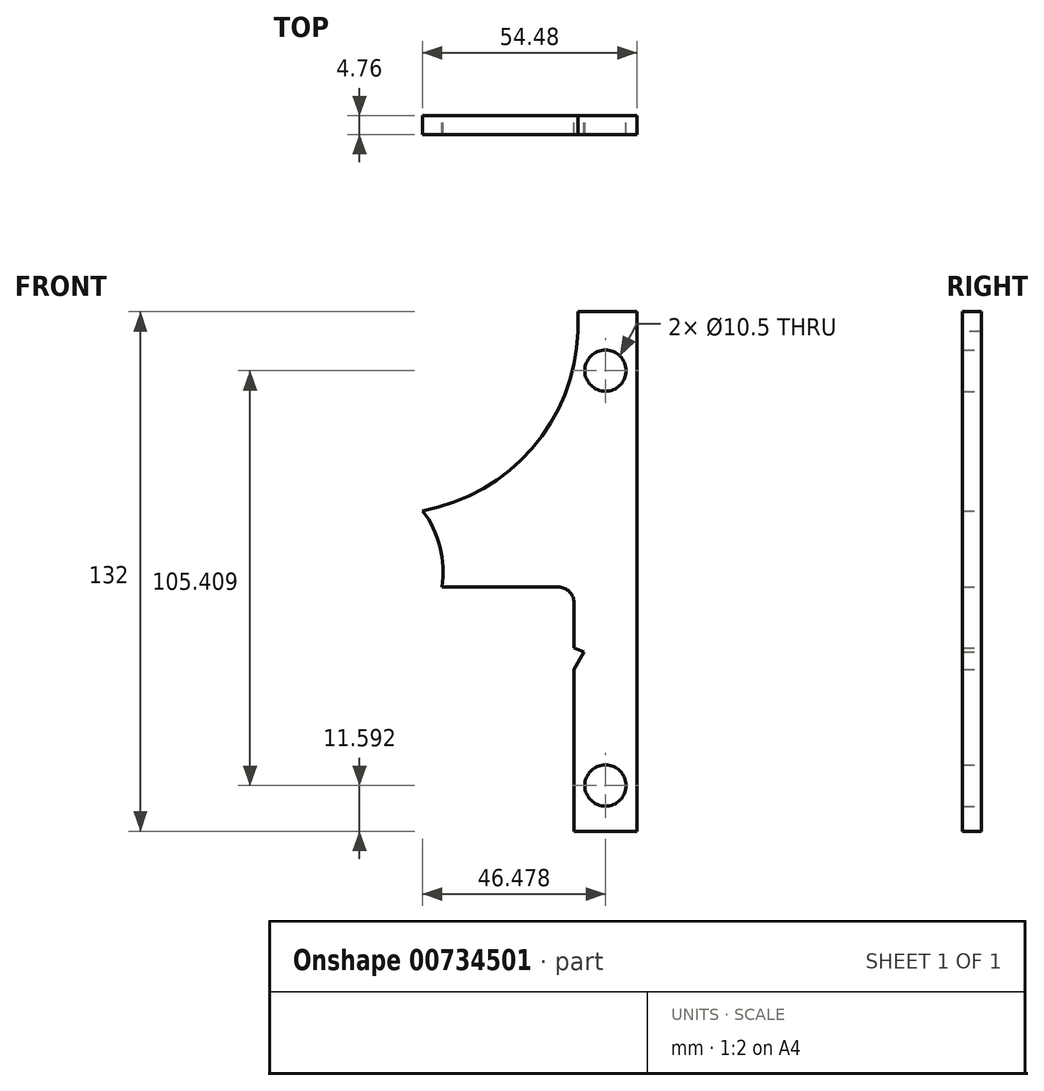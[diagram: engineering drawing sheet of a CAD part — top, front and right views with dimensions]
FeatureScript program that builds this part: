
annotation { "Feature Type Name" : "Feature", "Feature Type Description" : "" }
export const myFeature = defineFeature(function(context is Context, id is Id, definition is map)
    precondition{}
    {
        {
            var Q0;
            Q0=qCreatedBy(makeId("Front.planeOp"),FACE);
            var sketch = newSketch(context, id + "F0", { "sketchPlane" : qUnion([Q0])});
            skArc(sketch, "E0", {"start": v(12.24, 61) * mm, "mid": v(0.58, 31.2) * mm, "end": v(-27.24, 15.4) * mm});
            skArc(sketch, "E1", {"start": v(-27.24, 15.4) * mm, "mid": v(-22.78, 6.2) * mm, "end": v(-22.33, -4) * mm});
            skLineSegment(sketch, "E2", {"start": v(-22.33, -4) * mm, "end": v(7.24, -4) * mm});
            skArc(sketch, "E3", {"start": v(7.24, -4) * mm, "mid": v(10.07, -5.17) * mm, "end": v(11.24, -8) * mm});
            skLineSegment(sketch, "E4", {"start": v(11.24, -8) * mm, "end": v(11.24, -19.4) * mm});
            skLineSegment(sketch, "E5", {"start": v(11.24, -19.4) * mm, "end": v(13.74, -20.5) * mm});
            skLineSegment(sketch, "E6", {"start": v(13.74, -20.5) * mm, "end": v(11.24, -24.97) * mm});
            skLineSegment(sketch, "E7", {"start": v(11.24, -24.97) * mm, "end": v(11.24, -66) * mm});
            skLineSegment(sketch, "E8", {"start": v(11.24, -66) * mm, "end": v(27.24, -66) * mm});
            skLineSegment(sketch, "E9", {"start": v(27.24, -66) * mm, "end": v(27.24, 66) * mm});
            skLineSegment(sketch, "E10", {"start": v(27.24, 66) * mm, "end": v(12.24, 66) * mm});
            skLineSegment(sketch, "E11", {"start": v(12.24, 66) * mm, "end": v(12.24, 61) * mm});
            skCircle(sketch, "E12", {"center": v(19.24, 51) * mm, "radius": 5.25 * mm});
            skCircle(sketch, "E13", {"center": v(19.24, -54.4) * mm, "radius": 5.25 * mm});
            skSolve(sketch);
        }
        {
            var Q0;
            Q0 = qSketchRegion(id + "F0", true);
            extrude(context, id + "F1", {"entities" : qUnion([Q0]), "depth" : 4.76 * mm, "offsetDistance" : 25.4 * mm});
        }
    });
